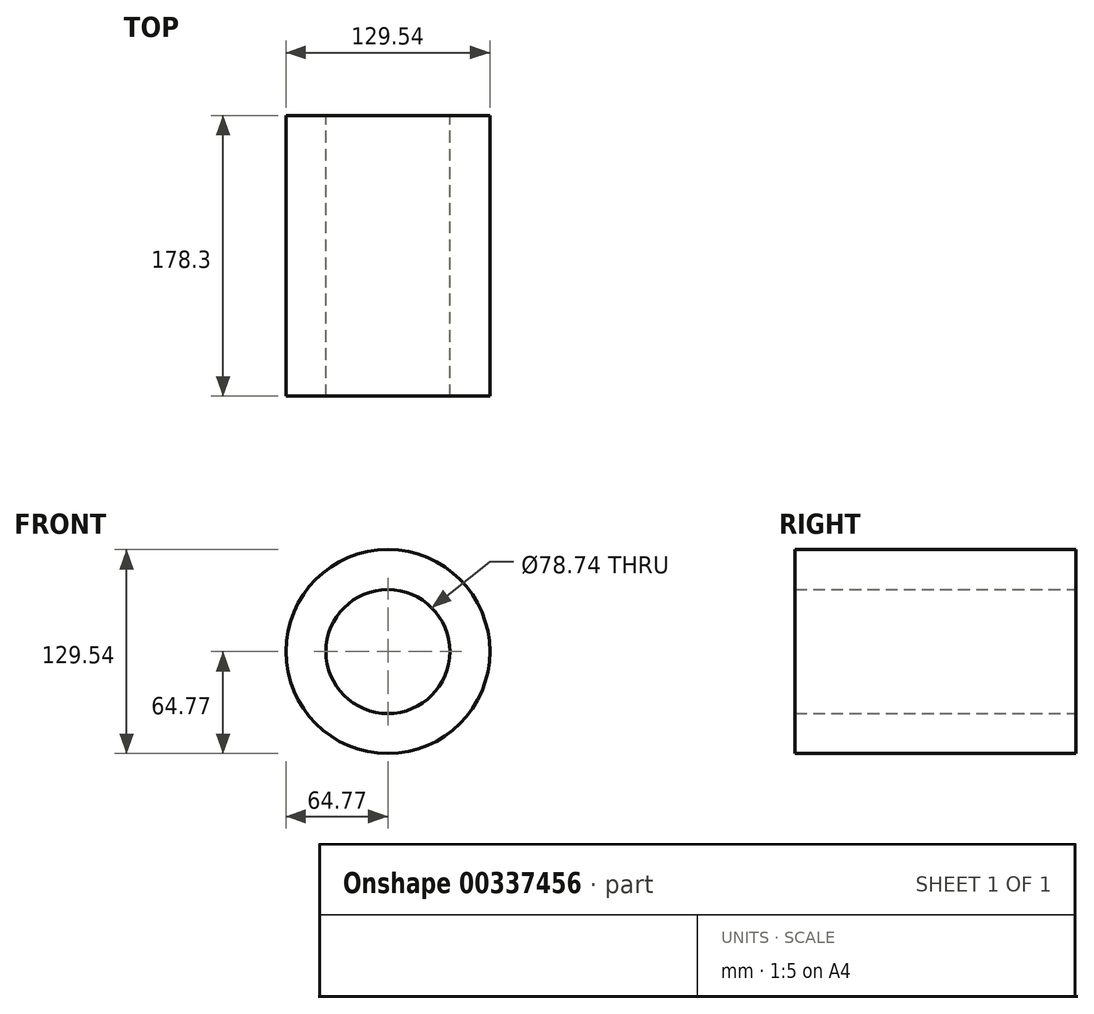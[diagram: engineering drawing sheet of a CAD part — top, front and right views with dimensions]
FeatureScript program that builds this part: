
annotation { "Feature Type Name" : "Feature", "Feature Type Description" : "" }
export const myFeature = defineFeature(function(context is Context, id is Id, definition is map)
    precondition{}
    {
        {
            var Q0;
            Q0=qCreatedBy(makeId("Front.planeOp"),FACE);
            var sketch = newSketch(context, id + "F0", { "sketchPlane" : qUnion([Q0])});
            skCircle(sketch, "E0", {"center": v(0, 0) * mm, "radius": 39.37 * mm});
            skCircle(sketch, "E1.0", {"center": v(0, 0) * mm, "radius": 64.77 * mm});
            skSolve(sketch);
        }
        {
            var Q0;
            Q0=makeQuery(id+"F0.imprint","IMPRINT",FACE,{"disambiguationData":[TD([[makeQuery(id+"F0.imprint","IMPRINT",EDGE,{"derivedFrom":sQuery(id+"F0.wireOp",EDGE,"E0")}),-1.0]])]});
            extrude(context, id + "F1", {"entities" : qUnion([Q0]), "endBound" : BoundingType.SYMMETRIC, "depth" : 178.3 * mm});
        }
    });
